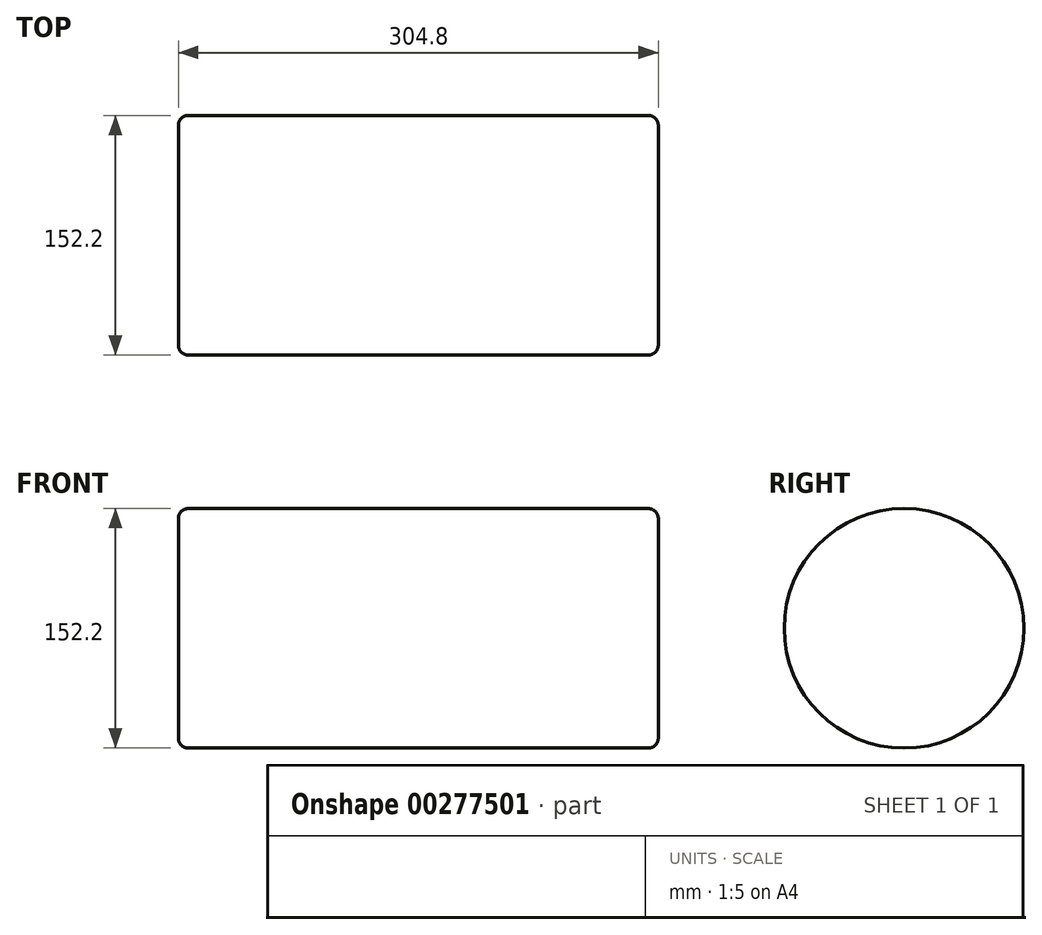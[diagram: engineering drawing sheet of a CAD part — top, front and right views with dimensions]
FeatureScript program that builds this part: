
annotation { "Feature Type Name" : "Feature", "Feature Type Description" : "" }
export const myFeature = defineFeature(function(context is Context, id is Id, definition is map)
    precondition{}
    {
        {
            var Q0;
            Q0=qCreatedBy(makeId("Right.planeOp"),FACE);
            var sketch = newSketch(context, id + "F0", { "sketchPlane" : qUnion([Q0])});
            skCircle(sketch, "E0", {"center": v(0, 0) * mm, "radius": 76.1 * mm});
            skSolve(sketch);
        }
        {
            var Q0;
            Q0 = qSketchRegion(id + "F0", true);
            extrude(context, id + "F1", {"entities" : qUnion([Q0]), "depth" : 152.4 * mm, "hasSecondDirection" : true, "secondDirectionOppositeDirection" : true, "secondDirectionDepth" : 152.4 * mm});
        }
        {
            var Q0;
            Q0=makeQuery(id+"F1.opExtrude","CAP_FACE",FACE,{"disambiguationData":[OSD([sQuery(id+"F0.wireOp",EDGE,"E0")])],"isStart":false});
            fillet(context, id + "F2", {"entities" : qUnion([Q0]), "radius" : 6.35 * mm, "tangentPropagation" : true, "allowEdgeOverflow" : false});
        }
        {
            var Q0;
            Q0=makeQuery(id+"F1.opExtrude","CAP_EDGE",EDGE,{"disambiguationData":[OSD([sQuery(id+"F0.wireOp",EDGE,"E0")])],"isStart":true});
            fillet(context, id + "F3", {"entities" : qUnion([Q0]), "radius" : 6.35 * mm, "tangentPropagation" : true, "allowEdgeOverflow" : false});
        }
    });
